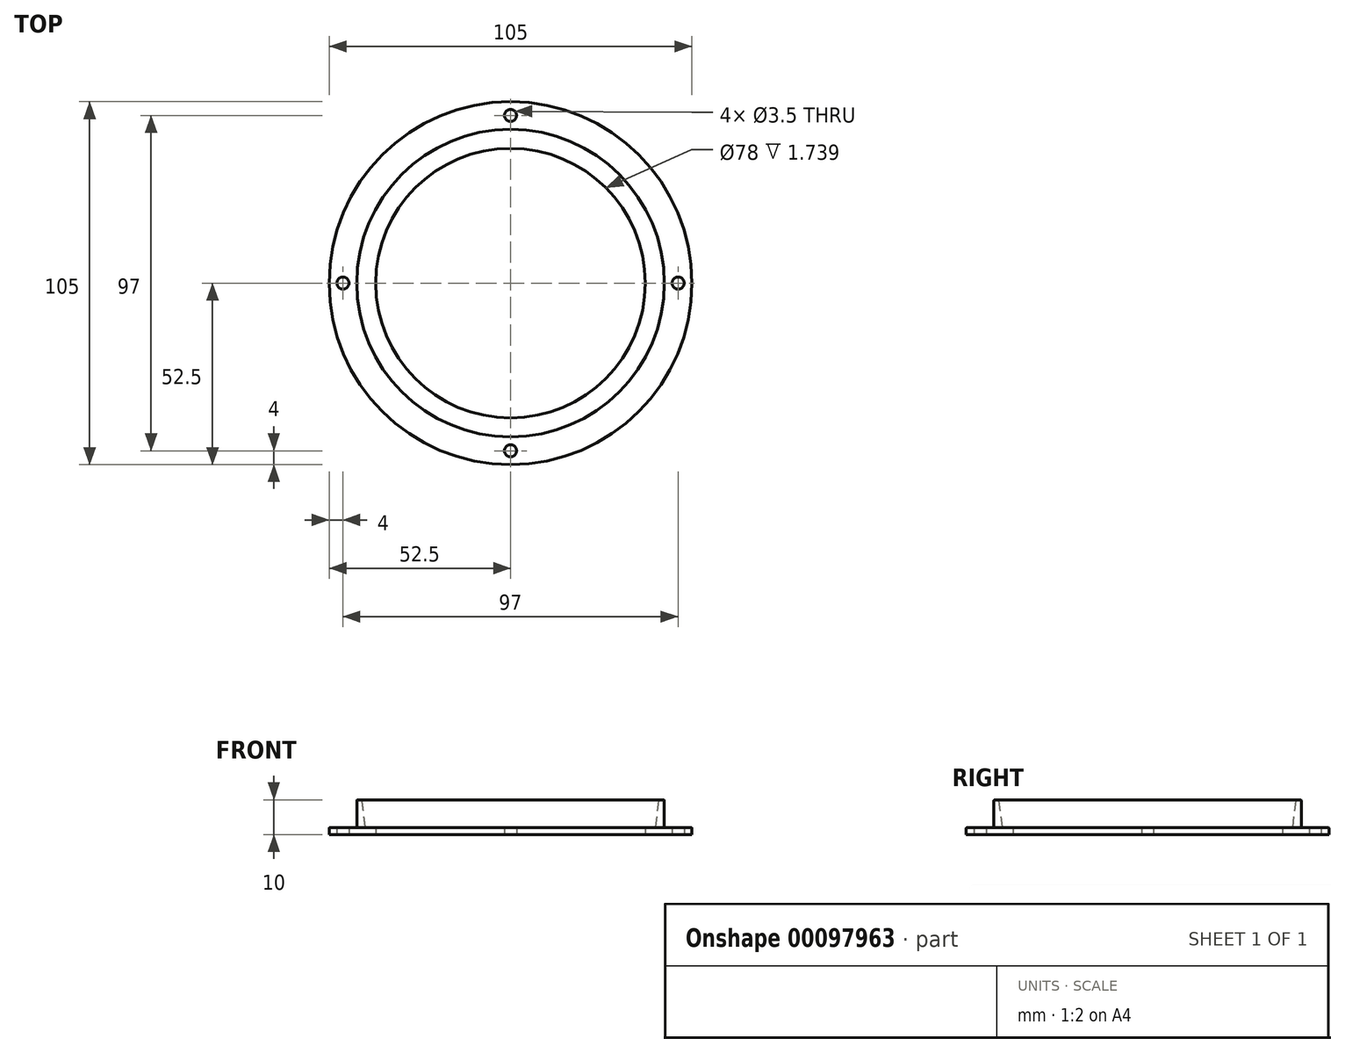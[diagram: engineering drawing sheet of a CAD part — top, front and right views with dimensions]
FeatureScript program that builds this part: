
annotation { "Feature Type Name" : "Feature", "Feature Type Description" : "" }
export const myFeature = defineFeature(function(context is Context, id is Id, definition is map)
    precondition{}
    {
        {
            var Q0;
            Q0=qCreatedBy(makeId("Front.planeOp"),FACE);
            var sketch = newSketch(context, id + "F0", { "sketchPlane" : qUnion([Q0])});
            skLineSegment(sketch, "E0", {"start": v(0, 0) * mm, "end": v(0, 47.7) * mm, "construction": true});
            skLineSegment(sketch, "E1", {"start": v(39, 0) * mm, "end": v(52.5, 0) * mm});
            skLineSegment(sketch, "E2", {"start": v(52.5, 0) * mm, "end": v(52.5, 2) * mm});
            skLineSegment(sketch, "E3", {"start": v(52.5, 2) * mm, "end": v(44.5, 2) * mm});
            skLineSegment(sketch, "E4", {"start": v(44.5, 2) * mm, "end": v(44.5, 10) * mm});
            skLineSegment(sketch, "E5", {"start": v(44.5, 10) * mm, "end": v(43, 10) * mm});
            skLineSegment(sketch, "E6", {"start": v(43, 10) * mm, "end": v(42, 2) * mm});
            skLineSegment(sketch, "E7", {"start": v(39, 0) * mm, "end": v(39, 1.99) * mm});
            skLineSegment(sketch, "E8", {"start": v(39, 1.99) * mm, "end": v(42, 2) * mm});
            skSolve(sketch);
        }
        {
            var Q0;
            Q0 = qSketchRegion(id + "F0", true);
            var Q1;
            Q1=sQuery(id+"F0.wireOp",EDGE,"E0");
            revolve(context, id + "F1", {"entities" : qUnion([Q0]), "axis" : qUnion([Q1]), "revolveType" : RevolveType.FULL});
        }
        {
            var Q0;
            Q0=makeQuery(id+"F1.opRevolve","SWEPT_EDGE",EDGE,{"disambiguationData":[OSD([sQuery(id+"F0.wireOp",EDGE,"E5"),sQuery(id+"F0.wireOp",EDGE,"E6")])]});
            var Q1;
            Q1=makeQuery(id+"F1.opRevolve","SWEPT_EDGE",EDGE,{"disambiguationData":[OSD([sQuery(id+"F0.wireOp",EDGE,"E4"),sQuery(id+"F0.wireOp",EDGE,"E5")])]});
            var Q2;
            Q2=makeQuery(id+"F1.opRevolve","SWEPT_EDGE",EDGE,{"disambiguationData":[OSD([sQuery(id+"F0.wireOp",EDGE,"E3"),sQuery(id+"F0.wireOp",EDGE,"E4")])]});
            var Q3;
            Q3=makeQuery(id+"F1.opRevolve","SWEPT_EDGE",EDGE,{"disambiguationData":[OSD([sQuery(id+"F0.wireOp",EDGE,"E2"),sQuery(id+"F0.wireOp",EDGE,"E3")])]});
            var Q4;
            Q4=makeQuery(id+"F1.opRevolve","SWEPT_EDGE",EDGE,{"disambiguationData":[OSD([sQuery(id+"F0.wireOp",EDGE,"E6"),sQuery(id+"F0.wireOp",EDGE,"E8")])]});
            var Q5;
            Q5=makeQuery(id+"F1.opRevolve","SWEPT_EDGE",EDGE,{"disambiguationData":[OSD([sQuery(id+"F0.wireOp",EDGE,"E7"),sQuery(id+"F0.wireOp",EDGE,"E8")])]});
            fillet(context, id + "F2", {"entities" : qUnion([Q0, Q1, Q2, Q3, Q4, Q5]), "radius" : 0.25 * mm, "tangentPropagation" : true, "allowEdgeOverflow" : false});
        }
        {
            var Q0;
            Q0=qCreatedBy(makeId("Top.planeOp"),FACE);
            var sketch = newSketch(context, id + "F3", { "sketchPlane" : qUnion([Q0])});
            skCircle(sketch, "E9", {"center": v(48.5, 0) * mm, "radius": 1.75 * mm});
            skCircle(sketch, "E10", {"center": v(0, 0) * mm, "radius": 48.5 * mm, "construction": true});
            skCircle(sketch, "E11", {"center": v(0, 48.5) * mm, "radius": 1.75 * mm});
            skCircle(sketch, "E12", {"center": v(-48.5, 0) * mm, "radius": 1.75 * mm});
            skCircle(sketch, "E13", {"center": v(0, -48.5) * mm, "radius": 1.75 * mm});
            skSolve(sketch);
        }
        {
            var Q0;
            Q0 = qSketchRegion(id + "F3", true);
            extrude(context, id + "F4", {"entities" : qUnion([Q0]), "operationType" : NewBodyOperationType.REMOVE, "endBound" : BoundingType.THROUGH_ALL, "depth" : 25 * mm});
        }
    });
